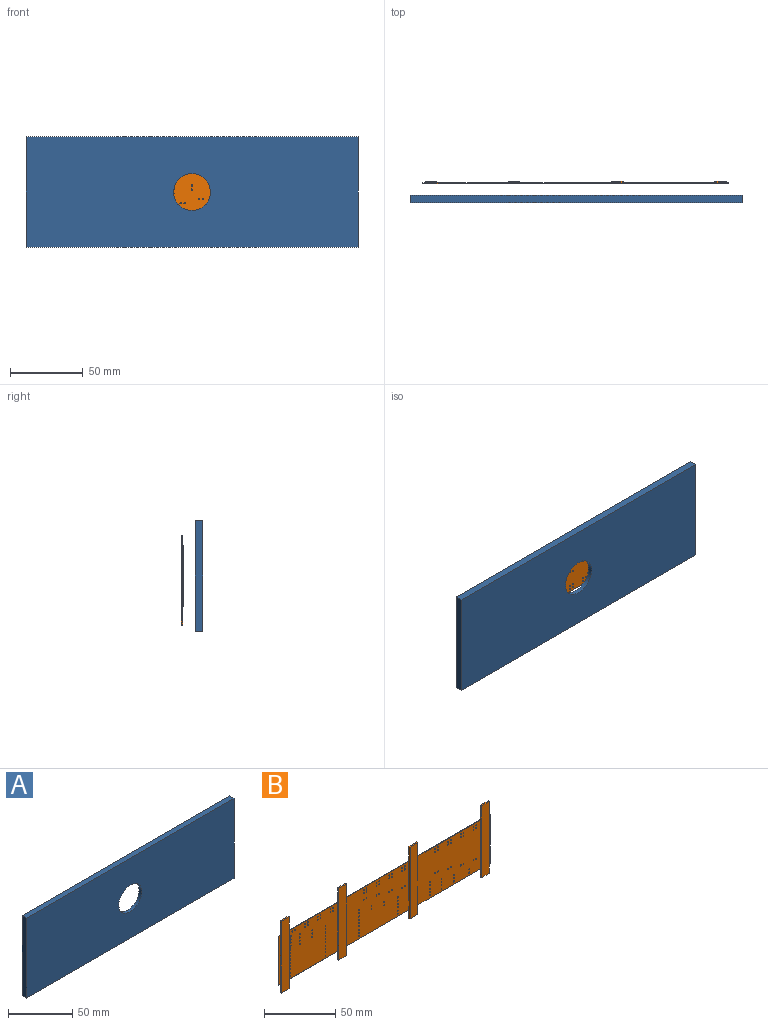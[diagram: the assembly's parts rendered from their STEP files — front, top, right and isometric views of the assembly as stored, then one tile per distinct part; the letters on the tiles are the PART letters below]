
ASSEMBLY  parts=2 mates=1
PART A: 60 faces, bbox 228.6x5.1x76.2 mm
  f0: plane 2.03x1.52mm, normal (0,0,-1), area 3.1mm2, adj f8,f16,f18,f33
  f1: plane 48.67x2.03mm, normal (0,0,-1), area 98.9mm2, adj f8,f18,f29,f32
  f2: plane 62.64x2.03mm, normal (0,0,-1), area 127.3mm2, adj f8,f18,f20,f28
  f3: plane 62.64x2.03mm, normal (0,0,-1), area 127.3mm2, adj f8,f18,f21,f25
  f4: plane 62.64x2.03mm, normal (0,0,1), area 127.3mm2, adj f8,f18,f35,f40
  f5: plane 62.64x2.03mm, normal (0,0,1), area 127.3mm2, adj f8,f18,f37,f45
  f6: plane 2.03x1.52mm, normal (0,0,1), area 3.1mm2, adj f8,f16,f18,f48
  f7: plane 48.67x2.03mm, normal (0,0,1), area 98.9mm2, adj f8,f18,f44,f49
  f8: plane 228.6x76.2mm, normal (0,1,0), area 7786mm2, adj f0,f1,f2,f3,f4,f5,f6,f7
  f9: plane 2.03x1.52mm, normal (0,0,1), area 3.1mm2, adj f8,f17,f18,f41
  f10: plane 2.03x1.52mm, normal (0,0,-1), area 3.1mm2, adj f8,f17,f18,f24
  f11: plane 228.6x5.08mm, normal (0,0,-1), area 1161.3mm2, adj f8,f12,f14,f15
  f12: plane 76.2x5.08mm, normal (1,0,0), area 387.1mm2, adj f8,f11,f13,f15
  f13: plane 228.6x5.08mm, normal (0,0,1), area 1161.3mm2, adj f8,f12,f14,f15
  f14: plane 76.2x5.08mm, normal (-1,0,0), area 387.1mm2, adj f8,f11,f13,f15
  f15: plane 228.6x76.2mm, normal (0,-1,0), area 16912.6mm2, adj f11,f12,f13,f14,f51
  f16: plane 42.47x2.03mm, normal (1,0,0), area 86.3mm2, adj f0,f6,f8,f18
  f17: plane 42.47x2.03mm, normal (-1,0,0), area 86.3mm2, adj f8,f9,f10,f18
  f18: plane 210.92x46.53mm, normal (0,1,0), area 8588.8mm2, adj f0,f1,f2,f3,f4,f5,f6,f7
  f19: plane 8.48x4.83mm, normal (0,1,0), area 40.9mm2, adj f20,f21,f22,f58
  f20: plane 7.37x2.03mm, normal (1,0,0), area 12.4mm2, adj f2,f8,f18,f19,f22,f58
  f21: plane 7.37x2.03mm, normal (-1,0,0), area 12.4mm2, adj f3,f8,f18,f19,f22,f58
  f22: plane 8.48x1.52mm, normal (0,0,-1), area 12.9mm2, adj f8,f19,f20,f21
  f23: plane 8.48x4.83mm, normal (0,1,0), area 40.9mm2, adj f24,f25,f26,f59
  f24: plane 7.37x2.03mm, normal (-1,0,0), area 12.4mm2, adj f8,f10,f18,f23,f26,f59
  f25: plane 7.37x2.03mm, normal (1,0,0), area 12.4mm2, adj f3,f8,f18,f23,f26,f59
  f26: plane 8.48x1.52mm, normal (0,0,-1), area 12.9mm2, adj f8,f23,f24,f25
  f27: plane 8.48x4.83mm, normal (0,1,0), area 40.9mm2, adj f28,f29,f30,f57
  f28: plane 7.37x2.03mm, normal (-1,0,0), area 12.4mm2, adj f2,f8,f18,f27,f30,f57
  f29: plane 7.37x2.03mm, normal (1,0,0), area 12.4mm2, adj f1,f8,f18,f27,f30,f57
  f30: plane 8.48x1.52mm, normal (0,0,-1), area 12.9mm2, adj f8,f27,f28,f29
  f31: plane 8.48x4.83mm, normal (0,1,0), area 40.9mm2, adj f32,f33,f34,f56
  f32: plane 7.37x2.03mm, normal (-1,0,0), area 12.4mm2, adj f1,f8,f18,f31,f34,f56
  f33: plane 7.37x2.03mm, normal (1,0,0), area 12.4mm2, adj f0,f8,f18,f31,f34,f56
  f34: plane 8.48x1.52mm, normal (0,0,-1), area 12.9mm2, adj f8,f31,f32,f33
  f35: plane 12.55x2.03mm, normal (-1,0,0), area 20.3mm2, adj f4,f8,f18,f36,f38,f53
  f36: plane 8.48x1.52mm, normal (0,0,1), area 12.9mm2, adj f8,f35,f37,f38
  f37: plane 12.55x2.03mm, normal (1,0,0), area 20.3mm2, adj f5,f8,f18,f36,f38,f53
  f38: plane 10.01x8.48mm, normal (0,1,0), area 84.9mm2, adj f35,f36,f37,f53
  f39: plane 8.48x1.52mm, normal (0,0,1), area 12.9mm2, adj f8,f40,f41,f42
  f40: plane 12.55x2.03mm, normal (1,0,0), area 20.3mm2, adj f4,f8,f18,f39,f42,f52
  f41: plane 12.55x2.03mm, normal (-1,0,0), area 20.3mm2, adj f8,f9,f18,f39,f42,f52
  f42: plane 10.01x8.48mm, normal (0,1,0), area 84.9mm2, adj f39,f40,f41,f52
  f43: plane 8.48x1.52mm, normal (0,0,1), area 12.9mm2, adj f8,f44,f45,f46
  f44: plane 12.55x2.03mm, normal (1,0,0), area 20.3mm2, adj f7,f8,f18,f43,f46,f55
  f45: plane 12.55x2.03mm, normal (-1,0,0), area 20.3mm2, adj f5,f8,f18,f43,f46,f55
  f46: plane 10.01x8.48mm, normal (0,1,0), area 84.9mm2, adj f43,f44,f45,f55
  f47: plane 8.48x1.52mm, normal (0,0,1), area 12.9mm2, adj f8,f48,f49,f50
  f48: plane 12.55x2.03mm, normal (1,0,0), area 20.3mm2, adj f6,f8,f18,f47,f50,f54
  f49: plane 12.55x2.03mm, normal (-1,0,0), area 20.3mm2, adj f7,f8,f18,f47,f50,f54
  f50: plane 10.01x8.48mm, normal (0,1,0), area 84.9mm2, adj f47,f48,f49,f54
  f51: cylinder r=12.7mm len=25.4mm, axis (0,-1,0), area 243.2mm2, adj f15,f18
  f52: plane 8.48x0.51mm, normal (0,0.71,0.71), area 6.1mm2, adj f18,f40,f41,f42
  f53: plane 8.48x0.51mm, normal (0,0.71,0.71), area 6.1mm2, adj f18,f35,f37,f38
  f54: plane 8.48x0.51mm, normal (0,0.71,0.71), area 6.1mm2, adj f18,f48,f49,f50
  f55: plane 8.48x0.51mm, normal (0,0.71,0.71), area 6.1mm2, adj f18,f44,f45,f46
  f56: plane 8.48x0.51mm, normal (0,0.71,-0.71), area 6.1mm2, adj f18,f31,f32,f33
  f57: plane 8.48x0.51mm, normal (0,0.71,-0.71), area 6.1mm2, adj f18,f27,f28,f29
  f58: plane 8.48x0.51mm, normal (0,0.71,-0.71), area 6.1mm2, adj f18,f19,f20,f21
  f59: plane 8.48x0.51mm, normal (0,0.71,-0.71), area 6.1mm2, adj f18,f23,f24,f25
PART B: 163 faces, bbox 210.5x1.5x61.9 mm
  f0: plane 210.52x42.06mm, normal (0,1,0), area 8776.6mm2, adj f21,f22,f23,f24,f30,f31,f32,f33
  f1: plane 7.93x1.02mm, normal (0,0,1), area 8.1mm2, adj f2,f4,f26,f162
  f2: plane 61.87x1.02mm, normal (1,0,0), area 62.9mm2, adj f1,f3,f20,f26,f161,f162
  f3: plane 7.93x1.02mm, normal (0,0,-1), area 8.1mm2, adj f2,f4,f26,f161
  f4: plane 61.87x1.02mm, normal (-1,0,0), area 62.9mm2, adj f1,f3,f18,f26,f161,f162
  f5: plane 7.93x1.02mm, normal (0,0,-1), area 8.1mm2, adj f6,f8,f27,f159
  f6: plane 61.87x1.02mm, normal (-1,0,0), area 62.9mm2, adj f5,f7,f20,f27,f159,f160
  f7: plane 7.93x1.02mm, normal (0,0,1), area 8.1mm2, adj f6,f8,f27,f160
  f8: plane 61.87x1.02mm, normal (1,0,0), area 62.9mm2, adj f5,f7,f19,f27,f159,f160
  f9: plane 7.93x1.02mm, normal (0,0,-1), area 8.1mm2, adj f10,f12,f28,f157
  f10: plane 61.87x1.02mm, normal (-1,0,0), area 62.9mm2, adj f9,f11,f17,f28,f157,f158
  f11: plane 7.93x1.02mm, normal (0,0,1), area 8.1mm2, adj f10,f12,f28,f158
  f12: plane 61.87x1.02mm, normal (1,0,0), area 62.9mm2, adj f9,f11,f18,f28,f157,f158
  f13: plane 7.93x1.02mm, normal (0,0,-1), area 8.1mm2, adj f14,f16,f29,f155
  f14: plane 61.87x1.02mm, normal (-1,0,0), area 62.9mm2, adj f13,f15,f25,f29,f155,f156
  f15: plane 7.93x1.02mm, normal (0,0,1), area 8.1mm2, adj f14,f16,f29,f156
  f16: plane 61.87x1.02mm, normal (1,0,0), area 62.9mm2, adj f13,f15,f17,f29,f155,f156
  f17: plane 49.23x42.06mm, normal (0,-1,0), area 2039.8mm2, adj f10,f16,f21,f23,f30,f45,f46,f55
  f18: plane 63.2x42.06mm, normal (0,-1,0), area 2633mm2, adj f4,f12,f21,f23,f37,f38,f39,f40
  f19: plane 42.06x1.6mm, normal (0,-1,0), area 67.3mm2, adj f8,f21,f22,f23
  f20: plane 63.2x42.06mm, normal (0,-1,0), area 2635.9mm2, adj f2,f6,f21,f23,f31,f32,f33,f34
  f21: plane 210.52x0.51mm, normal (0,0,-1), area 106.9mm2, adj f0,f17,f18,f19,f20,f22,f24,f25
  f22: plane 42.06x0.51mm, normal (1,0,0), area 21.4mm2, adj f0,f19,f21,f23
  f23: plane 210.52x0.51mm, normal (0,0,1), area 106.9mm2, adj f0,f17,f18,f19,f20,f22,f24,f25
  f24: plane 42.06x0.51mm, normal (-1,0,0), area 21.4mm2, adj f0,f21,f23,f25
  f25: plane 42.06x1.6mm, normal (0,-1,0), area 67.3mm2, adj f14,f21,f23,f24
  f26: plane 61.87x7.93mm, normal (0,-1,0), area 490.3mm2, adj f1,f2,f3,f4
  f27: plane 61.87x7.93mm, normal (0,-1,0), area 490.3mm2, adj f5,f6,f7,f8
  f28: plane 61.87x7.93mm, normal (0,-1,0), area 490.3mm2, adj f9,f10,f11,f12
  f29: plane 61.87x7.93mm, normal (0,-1,0), area 490.3mm2, adj f13,f14,f15,f16
  f30: cylinder r=0.43mm len=0.86mm, axis (0,-1,0), area 1.4mm2, adj f0,f17
  f31: cylinder r=0.43mm len=0.86mm, axis (0,-1,0), area 1.4mm2, adj f0,f20
  f32: cylinder r=0.43mm len=0.86mm, axis (0,-1,0), area 1.4mm2, adj f0,f20
  f33: cylinder r=0.43mm len=0.86mm, axis (0,-1,0), area 1.4mm2, adj f0,f20
  f34: cylinder r=0.43mm len=0.86mm, axis (0,-1,0), area 1.4mm2, adj f0,f20
  f35: cylinder r=0.43mm len=0.86mm, axis (0,-1,0), area 1.4mm2, adj f0,f20
  f36: cylinder r=0.43mm len=0.86mm, axis (0,-1,0), area 1.4mm2, adj f0,f20
  f37: cylinder r=0.43mm len=0.86mm, axis (0,-1,0), area 1.4mm2, adj f0,f18
  f38: cylinder r=0.43mm len=0.86mm, axis (0,-1,0), area 1.4mm2, adj f0,f18
  f39: cylinder r=0.43mm len=0.86mm, axis (0,-1,0), area 1.4mm2, adj f0,f18
  f40: cylinder r=0.43mm len=0.86mm, axis (0,-1,0), area 1.4mm2, adj f0,f18
  f41: cylinder r=0.43mm len=0.86mm, axis (0,-1,0), area 1.4mm2, adj f0,f18
  f42: cylinder r=0.43mm len=0.86mm, axis (0,-1,0), area 1.4mm2, adj f0,f18
  f43: cylinder r=0.43mm len=0.86mm, axis (0,-1,0), area 1.4mm2, adj f0,f18
  f44: cylinder r=0.43mm len=0.86mm, axis (0,-1,0), area 1.4mm2, adj f0,f18
  f45: cylinder r=0.43mm len=0.86mm, axis (0,-1,0), area 1.4mm2, adj f0,f17
  f46: cylinder r=0.43mm len=0.86mm, axis (0,-1,0), area 1.4mm2, adj f0,f17
  f47: cylinder r=0.43mm len=0.86mm, axis (0,-1,0), area 1.4mm2, adj f0,f18
  f48: cylinder r=0.43mm len=0.86mm, axis (0,-1,0), area 1.4mm2, adj f0,f20
  f49: cylinder r=0.43mm len=0.86mm, axis (0,-1,0), area 1.4mm2, adj f0,f20
  f50: cylinder r=0.43mm len=0.86mm, axis (0,-1,0), area 1.4mm2, adj f0,f20
  f51: cylinder r=0.43mm len=0.86mm, axis (0,-1,0), area 1.4mm2, adj f0,f18
  f52: cylinder r=0.43mm len=0.86mm, axis (0,-1,0), area 1.4mm2, adj f0,f18
  f53: cylinder r=0.43mm len=0.86mm, axis (0,-1,0), area 1.4mm2, adj f0,f18
  f54: cylinder r=0.43mm len=0.86mm, axis (0,-1,0), area 1.4mm2, adj f0,f18
  f55: cylinder r=0.43mm len=0.86mm, axis (0,-1,0), area 1.4mm2, adj f0,f17
  f56: cylinder r=0.43mm len=0.86mm, axis (0,-1,0), area 1.4mm2, adj f0,f17
  f57: cylinder r=0.43mm len=0.86mm, axis (0,-1,0), area 1.4mm2, adj f0,f17
  f58: cylinder r=0.43mm len=0.86mm, axis (0,-1,0), area 1.4mm2, adj f0,f17
  f59: cylinder r=0.43mm len=0.86mm, axis (0,-1,0), area 1.4mm2, adj f0,f20
  f60: cylinder r=0.43mm len=0.86mm, axis (0,-1,0), area 1.4mm2, adj f0,f20
  f61: cylinder r=0.43mm len=0.86mm, axis (0,-1,0), area 1.4mm2, adj f0,f20
  f62: cylinder r=0.43mm len=0.86mm, axis (0,-1,0), area 1.4mm2, adj f0,f17
  f63: cylinder r=0.43mm len=0.86mm, axis (0,-1,0), area 1.4mm2, adj f0,f18
  f64: cylinder r=0.43mm len=0.86mm, axis (0,-1,0), area 1.4mm2, adj f0,f18
  f65: cylinder r=0.43mm len=0.86mm, axis (0,-1,0), area 1.4mm2, adj f0,f18
  f66: cylinder r=0.43mm len=0.86mm, axis (0,-1,0), area 1.4mm2, adj f0,f18
  f67: cylinder r=0.43mm len=0.86mm, axis (0,-1,0), area 1.4mm2, adj f0,f20
  f68: cylinder r=0.43mm len=0.86mm, axis (0,-1,0), area 1.4mm2, adj f0,f20
  f69: cylinder r=0.43mm len=0.86mm, axis (0,-1,0), area 1.4mm2, adj f0,f20
  f70: cylinder r=0.43mm len=0.86mm, axis (0,-1,0), area 1.4mm2, adj f0,f20
  f71: cylinder r=0.43mm len=0.86mm, axis (0,-1,0), area 1.4mm2, adj f0,f20
  f72: cylinder r=0.43mm len=0.86mm, axis (0,-1,0), area 1.4mm2, adj f0,f20
  f73: cylinder r=0.43mm len=0.86mm, axis (0,-1,0), area 1.4mm2, adj f0,f20
  f74: cylinder r=0.43mm len=0.86mm, axis (0,-1,0), area 1.4mm2, adj f0,f20
  f75: cylinder r=0.43mm len=0.86mm, axis (0,-1,0), area 1.4mm2, adj f0,f20
  f76: cylinder r=0.43mm len=0.86mm, axis (0,-1,0), area 1.4mm2, adj f0,f20
  f77: cylinder r=0.43mm len=0.86mm, axis (0,-1,0), area 1.4mm2, adj f0,f17
  f78: cylinder r=0.43mm len=0.86mm, axis (0,-1,0), area 1.4mm2, adj f0,f17
  f79: cylinder r=0.43mm len=0.86mm, axis (0,-1,0), area 1.4mm2, adj f0,f17
  f80: cylinder r=0.43mm len=0.86mm, axis (0,-1,0), area 1.4mm2, adj f0,f17
  f81: cylinder r=0.43mm len=0.86mm, axis (0,-1,0), area 1.4mm2, adj f0,f17
  f82: cylinder r=0.43mm len=0.86mm, axis (0,-1,0), area 1.4mm2, adj f0,f17
  f83: cylinder r=0.43mm len=0.86mm, axis (0,-1,0), area 1.4mm2, adj f0,f18
  f84: cylinder r=0.43mm len=0.86mm, axis (0,-1,0), area 1.4mm2, adj f0,f18
  f85: cylinder r=0.43mm len=0.86mm, axis (0,-1,0), area 1.4mm2, adj f0,f18
  f86: cylinder r=0.43mm len=0.86mm, axis (0,-1,0), area 1.4mm2, adj f0,f18
  f87: cylinder r=0.43mm len=0.86mm, axis (0,-1,0), area 1.4mm2, adj f0,f18
  f88: cylinder r=0.43mm len=0.86mm, axis (0,-1,0), area 1.4mm2, adj f0,f18
  f89: cylinder r=0.43mm len=0.86mm, axis (0,-1,0), area 1.4mm2, adj f0,f18
  f90: cylinder r=0.43mm len=0.86mm, axis (0,-1,0), area 1.4mm2, adj f0,f18
  f91: cylinder r=0.43mm len=0.86mm, axis (0,-1,0), area 1.4mm2, adj f0,f17
  f92: cylinder r=0.43mm len=0.86mm, axis (0,-1,0), area 1.4mm2, adj f0,f17
  f93: cylinder r=0.43mm len=0.86mm, axis (0,-1,0), area 1.4mm2, adj f0,f17
  f94: cylinder r=0.43mm len=0.86mm, axis (0,-1,0), area 1.4mm2, adj f0,f17
  f95: cylinder r=0.43mm len=0.86mm, axis (0,-1,0), area 1.4mm2, adj f0,f17
  f96: cylinder r=0.43mm len=0.86mm, axis (0,-1,0), area 1.4mm2, adj f0,f17
  f97: cylinder r=0.43mm len=0.86mm, axis (0,-1,0), area 1.4mm2, adj f0,f17
  f98: cylinder r=0.43mm len=0.86mm, axis (0,-1,0), area 1.4mm2, adj f0,f17
  f99: cylinder r=0.76mm len=1.52mm, axis (0,-1,0), area 2.4mm2, adj f0,f17
  f100: cylinder r=0.76mm len=1.52mm, axis (0,-1,0), area 2.4mm2, adj f0,f17
  f101: cylinder r=0.76mm len=1.52mm, axis (0,-1,0), area 2.4mm2, adj f0,f17
  f102: cylinder r=0.76mm len=1.52mm, axis (0,-1,0), area 2.4mm2, adj f0,f17
  f103: cylinder r=0.43mm len=0.86mm, axis (0,-1,0), area 1.4mm2, adj f0,f18
  f104: cylinder r=0.43mm len=0.86mm, axis (0,-1,0), area 1.4mm2, adj f0,f18
  f105: cylinder r=0.43mm len=0.86mm, axis (0,-1,0), area 1.4mm2, adj f0,f18
  f106: cylinder r=0.43mm len=0.86mm, axis (0,-1,0), area 1.4mm2, adj f0,f18
  f107: cylinder r=0.43mm len=0.86mm, axis (0,-1,0), area 1.4mm2, adj f0,f20
  f108: cylinder r=0.43mm len=0.86mm, axis (0,-1,0), area 1.4mm2, adj f0,f17
  f109: cylinder r=0.43mm len=0.86mm, axis (0,-1,0), area 1.4mm2, adj f0,f17
  f110: cylinder r=0.43mm len=0.86mm, axis (0,-1,0), area 1.4mm2, adj f0,f17
  f111: cylinder r=0.43mm len=0.86mm, axis (0,-1,0), area 1.4mm2, adj f0,f17
  f112: cylinder r=0.43mm len=0.86mm, axis (0,-1,0), area 1.4mm2, adj f0,f20
  f113: cylinder r=0.43mm len=0.86mm, axis (0,-1,0), area 1.4mm2, adj f0,f20
  f114: cylinder r=0.43mm len=0.86mm, axis (0,-1,0), area 1.4mm2, adj f0,f20
  f115: cylinder r=0.43mm len=0.86mm, axis (0,-1,0), area 1.4mm2, adj f0,f17
  f116: cylinder r=0.43mm len=0.86mm, axis (0,-1,0), area 1.4mm2, adj f0,f17
  f117: cylinder r=0.43mm len=0.86mm, axis (0,-1,0), area 1.4mm2, adj f0,f17
  f118: cylinder r=0.43mm len=0.86mm, axis (0,-1,0), area 1.4mm2, adj f0,f17
  f119: cylinder r=0.43mm len=0.86mm, axis (0,-1,0), area 1.4mm2, adj f0,f17
  f120: cylinder r=0.43mm len=0.86mm, axis (0,-1,0), area 1.4mm2, adj f0,f17
  f121: cylinder r=0.43mm len=0.86mm, axis (0,-1,0), area 1.4mm2, adj f0,f17
  f122: cylinder r=0.43mm len=0.86mm, axis (0,-1,0), area 1.4mm2, adj f0,f17
  f123: cylinder r=0.43mm len=0.86mm, axis (0,-1,0), area 1.4mm2, adj f0,f17
  f124: cylinder r=0.43mm len=0.86mm, axis (0,-1,0), area 1.4mm2, adj f0,f20
  f125: cylinder r=0.43mm len=0.86mm, axis (0,-1,0), area 1.4mm2, adj f0,f20
  f126: cylinder r=0.43mm len=0.86mm, axis (0,-1,0), area 1.4mm2, adj f0,f20
  f127: cylinder r=0.43mm len=0.86mm, axis (0,-1,0), area 1.4mm2, adj f0,f20
  f128: cylinder r=0.43mm len=0.86mm, axis (0,-1,0), area 1.4mm2, adj f0,f20
  f129: cylinder r=0.43mm len=0.86mm, axis (0,-1,0), area 1.4mm2, adj f0,f20
  f130: cylinder r=0.43mm len=0.86mm, axis (0,-1,0), area 1.4mm2, adj f0,f20
  f131: cylinder r=0.43mm len=0.86mm, axis (0,-1,0), area 1.4mm2, adj f0,f17
  f132: cylinder r=0.43mm len=0.86mm, axis (0,-1,0), area 1.4mm2, adj f0,f18
  f133: cylinder r=0.43mm len=0.86mm, axis (0,-1,0), area 1.4mm2, adj f0,f18
  f134: cylinder r=0.43mm len=0.86mm, axis (0,-1,0), area 1.4mm2, adj f0,f18
  f135: cylinder r=0.43mm len=0.86mm, axis (0,-1,0), area 1.4mm2, adj f0,f17
  f136: cylinder r=0.43mm len=0.86mm, axis (0,-1,0), area 1.4mm2, adj f0,f17
  f137: cylinder r=0.43mm len=0.86mm, axis (0,-1,0), area 1.4mm2, adj f0,f17
  f138: cylinder r=0.43mm len=0.86mm, axis (0,-1,0), area 1.4mm2, adj f0,f17
  f139: cylinder r=0.43mm len=0.86mm, axis (0,-1,0), area 1.4mm2, adj f0,f18
  f140: cylinder r=0.43mm len=0.86mm, axis (0,-1,0), area 1.4mm2, adj f0,f18
  f141: cylinder r=0.43mm len=0.86mm, axis (0,-1,0), area 1.4mm2, adj f0,f18
  f142: cylinder r=0.43mm len=0.86mm, axis (0,-1,0), area 1.4mm2, adj f0,f18
  f143: cylinder r=0.43mm len=0.86mm, axis (0,-1,0), area 1.4mm2, adj f0,f18
  f144: cylinder r=0.43mm len=0.86mm, axis (0,-1,0), area 1.4mm2, adj f0,f18
  f145: cylinder r=0.43mm len=0.86mm, axis (0,-1,0), area 1.4mm2, adj f0,f18
  f146: cylinder r=0.43mm len=0.86mm, axis (0,-1,0), area 1.4mm2, adj f0,f18
  f147: cylinder r=0.43mm len=0.86mm, axis (0,-1,0), area 1.4mm2, adj f0,f20
  f148: cylinder r=0.43mm len=0.86mm, axis (0,-1,0), area 1.4mm2, adj f0,f20
  f149: cylinder r=0.43mm len=0.86mm, axis (0,-1,0), area 1.4mm2, adj f0,f20
  f150: cylinder r=0.43mm len=0.86mm, axis (0,-1,0), area 1.4mm2, adj f0,f20
  f151: cylinder r=0.43mm len=0.86mm, axis (0,-1,0), area 1.4mm2, adj f0,f18
  f152: cylinder r=0.43mm len=0.86mm, axis (0,-1,0), area 1.4mm2, adj f0,f18
  f153: cylinder r=0.43mm len=0.86mm, axis (0,-1,0), area 1.4mm2, adj f0,f18
  f154: cylinder r=0.43mm len=0.86mm, axis (0,-1,0), area 1.4mm2, adj f0,f20
  f155: plane 7.93x7.11mm, normal (0,1,0), area 56.4mm2, adj f13,f14,f16,f21
  f156: plane 12.7x7.93mm, normal (0,1,0), area 100.6mm2, adj f14,f15,f16,f23
  f157: plane 7.93x7.11mm, normal (0,1,0), area 56.4mm2, adj f9,f10,f12,f21
  f158: plane 12.7x7.93mm, normal (0,1,0), area 100.6mm2, adj f10,f11,f12,f23
  f159: plane 7.93x7.11mm, normal (0,1,0), area 56.4mm2, adj f5,f6,f8,f21
  f160: plane 12.7x7.93mm, normal (0,1,0), area 100.6mm2, adj f6,f7,f8,f23
  f161: plane 7.93x7.11mm, normal (0,1,0), area 56.4mm2, adj f2,f3,f4,f21
  f162: plane 12.7x7.93mm, normal (0,1,0), area 100.6mm2, adj f1,f2,f4,f23
PLACE A at identity fixed
PLACE B rot(axis=(1,0,0),180deg) t=(-0.12,8.13,-0.03)mm
MATE slider A.f51 <-> B.f0  axis (0,1,0) through (0,-2.03,0)mm
